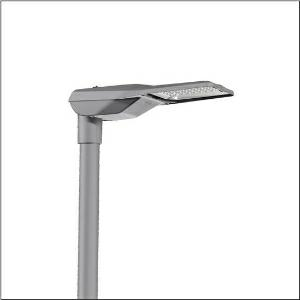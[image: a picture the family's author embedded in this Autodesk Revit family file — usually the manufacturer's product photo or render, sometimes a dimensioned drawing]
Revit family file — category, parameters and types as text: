
# Revit family: streetlight_sl_21_iq_mini___p0_8a_5xe2u31v08jb_63ec
name_source: partatom
category: Lighting Fixtures
units: mm (PartAtom-declared; Revit-internal decimal feet)

## family parameters
Cut with Voids When Loaded = No
Host = Face
Light Source = No
Part Type = Normal
Room Calculation Point = No
Round Connector Dimension = Use Diameter
Shared = No

## types (1)
- --- (1 x LED, 11310 lm, 72.5 W, 3000K)
    Apparent Load = 73 VA
    CIE Flux Codes = 36 69 97 100 100
    Color Rendering = 70
    Color Temperature = 3000K
    Default Elevation = 1800 mm
    Description = Streetlight SL 21 iQ mini, mast luminaire, primary light control with lens, of PMMA, primary optical cover: cover, of toughened safety glass, transparent, light distribution: P0.8a, light emission: direct distribution, primary light characteristic: asymmetric, installation type: post-top, side-entry, LED, High Power LED, rated luminous flux: 11.310lm, luminous efficacy: 156lm/W, light colour: 730, colour temperature: 3000K, control gear: iQ-Street Remote, D4i with power reduction, control: pre-setting: logarithmic dimming characteristic, Street-Remote, Auto-Match, Temp-Guard, Lumen-Switch, Night-Set, Smart-Wire, Light-Fading, Desk-Remote (wireless, voltage-free reading and setting of iQ features in the workshop via application-optimized NFC function/RFID function), optimised constant luminous flux control (CLO 2.0), mains connection: 220..240V, AC, 50/60Hz, start of lifetime: 73W, end of service life: 76W, reduction: 33W, luminaire housing, of diecast aluminium, powder-coated, Siteco® metallic grey (DB 702S), corrosivity category C5 mid according to DIN EN ISO 12944, please order mast flange separately, inclination adjustable: 0°, 5°, 10°, 15°, sealing non-destructively replaceable, multi-level sealing system, length: 628mm, width: 235mm, height: 110mm, mast flange for spigot size: 42mm (side-entry): 5XC10008XM4, 60/48mm (side-entry/post-top): 5XC10108XM2, 76/60mm (side-entry/post-top): 5XC10108XM1, mounting height: 4..8m, Smart Interface above, protection rating (complete): IP66, insulation class (complete): insulation class II (safety insulation), certification: CE, ENEC, ENEC+, VDE, impact resistance: IK09, permissible operating ambient temperature for outdoor applications: -40..+50°C, standard-compliant lighting for roads and squares, packaging unit: 1 piece

Light Distribution: P0.8a
    Height = 110 mm
    Lamp = 1 x LED
    Lamp Light Flux = 11310 lm
    Lamp Power = 72.5 W
    Lamp count = 1
    Length = 625 mm
    Luminous efficacy = 156 lm/W
    Manufacturer = Siteco
    ModVariant = No
    Model = 5XE2U31V08JB
    Number of Poles = 1
    OnlyDefault = Yes
    Power Factor = 1
    Product Name = Streetlight SL 21 iQ mini | P0.8a
    Product group = mast luminaire | pylon top
    ProductGroupID = 6100
    Protection Class = Protection class II
    Protection Degree = IP 66
    RLX_Detail_Level = 1
    RLX_Emergency_Light_Flux = 0 lm
    RLX_Emergency_Type = 0
    RLX_Emergency_Type_DB = No
    RlxData = <blob elided: 92349 chars, md5=6cdf9fd1>
    Socket = socket
    Standby Power = 0 W
    System Light Flux = 11310 lm
    System Power = 73 W
    Type Comments = factory setting: luminous flux: 100 % | dim-lin: 254 | 755 mA
    Type Image = l_1003515.jpg
    URL = http://relux.com
    VarID = @adj_069104
    Voltage = 0 V
    Weight = 0.00 kg
    Width = 234 mm

## geometry (parser evidence)
native form markers: Blend x4, Sweep x10
no freeform markers — native parametric forms only
